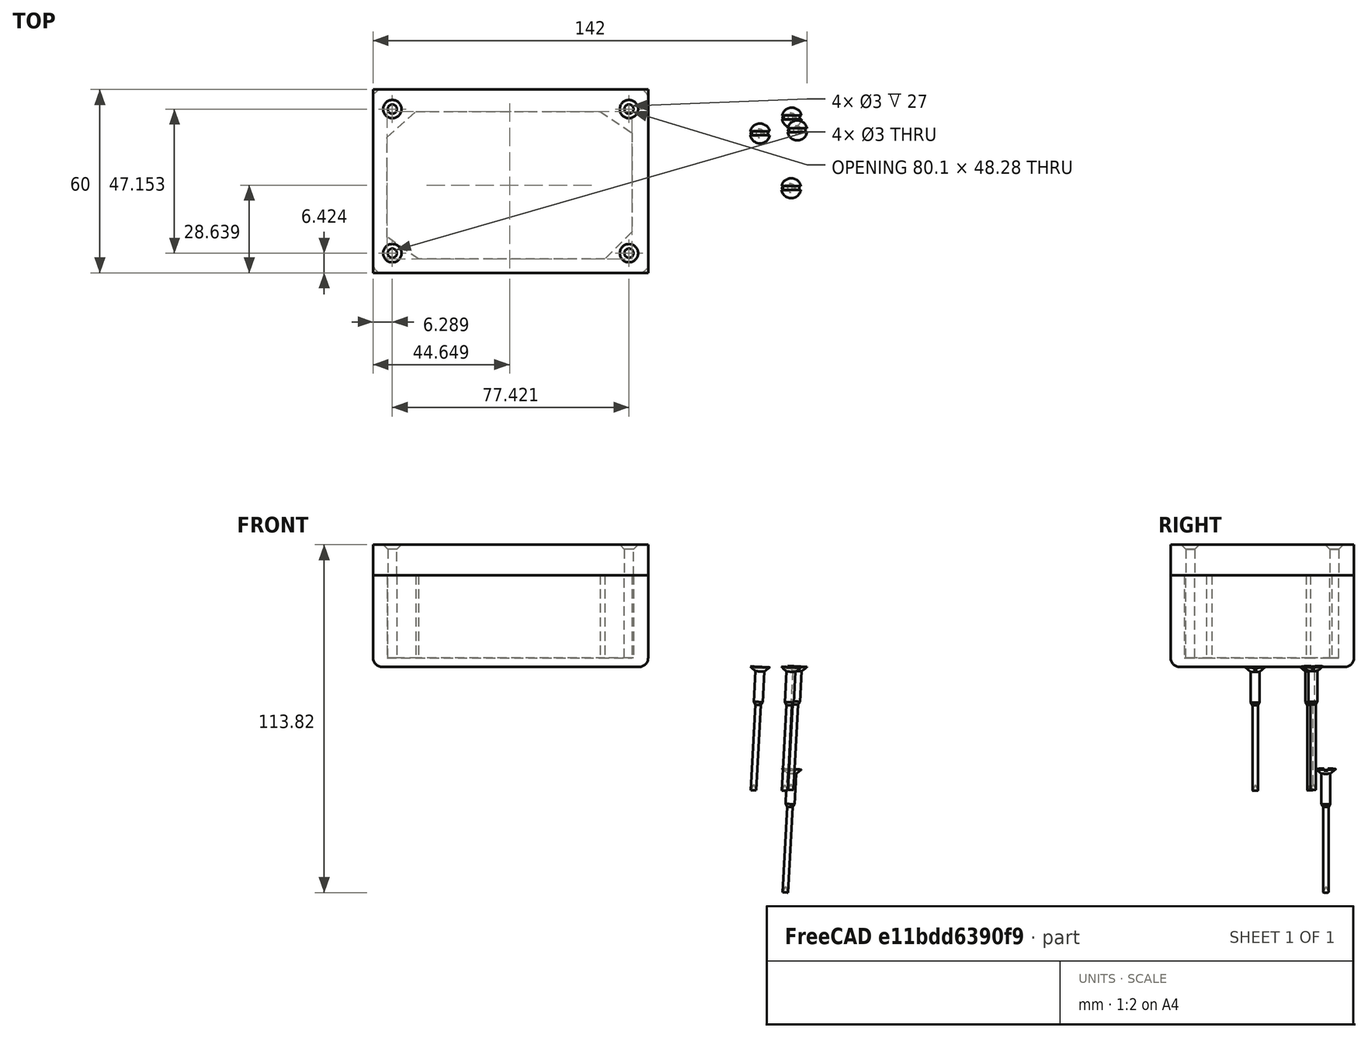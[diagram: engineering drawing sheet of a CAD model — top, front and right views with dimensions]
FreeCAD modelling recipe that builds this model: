
FCSTD DOCUMENT  (FreeCAD 0.18.4R)
Label: plastic_case3
License: All rights reserved
LicenseURL: http://en.wikipedia.org/wiki/All_rights_reserved
objects: Sketcher::SketchObject×16, TechDraw::DrawViewDimension×8, PartDesign::Body×7, PartDesign::Pocket×7, PartDesign::Revolution×4, TechDraw::DrawViewPart×3, PartDesign::Pad×2, PartDesign::Fillet×2, PartDesign::ShapeBinder×1, PartDesign::Chamfer×1, TechDraw::DrawSVGTemplate×1, TechDraw::DrawViewAnnotation×1, TechDraw::DrawPage×1
note: 53 computed .brp shape members not serialized (recipe doc carries the construction recipe); baked Part::Feature solids carry a one-line shape summary decoded from their .brp

FEATURE [Sketcher::SketchObject] Sketch
  MapMode = 5
  Support = -> [XY_Plane]
  sketch-geometry (4):
    g0: LineSegment StartX=-45 StartY=30 StartZ=0 EndX=45 EndY=30 EndZ=0
    g1: LineSegment StartX=45 StartY=30 StartZ=0 EndX=45 EndY=-30 EndZ=0
    g2: LineSegment StartX=45 StartY=-30 StartZ=0 EndX=-45 EndY=-30 EndZ=0
    g3: LineSegment StartX=-45 StartY=-30 StartZ=0 EndX=-45 EndY=30 EndZ=0
  constraints (12):
    c: Coincident(g0,g1)
    c: Coincident(g1,g2)
    c: Coincident(g2,g3)
    c: Coincident(g3,g0)
    c: Horizontal(g0)
    c: Horizontal(g2)
    c: Vertical(g1)
    c: Vertical(g3)
    c: DistanceX(g0) = 45
    c: DistanceY(g0) = 30
    c: DistanceX(g0,g0) = 90
    c: DistanceY(g1,g0) = 60
FEATURE [PartDesign::Pad] Pad
  Length = 30
  Length2 = 100
  Profile = -> Sketch
  Type = 0
FEATURE [PartDesign::ShapeBinder] CopyPad
  Placement = pos=(0,0,30) rot=(0,0,1;0rad)
  TraceSupport = false
FEATURE [Sketcher::SketchObject] Sketch001
  MapMode = 5
  Placement = pos=(0,0,30) rot=(0,0,1;0rad)
  Support = -> [CopyPad]
  sketch-geometry (12):
    g0: LineSegment StartX=-40.4009 StartY=14.4063 StartZ=0 EndX=-31.033 EndY=22.7794 EndZ=0
    g1: LineSegment StartX=-31.033 StartY=22.7794 StartZ=0 EndX=29.2768 EndY=22.7794 EndZ=0
    g2: LineSegment StartX=29.2768 StartY=22.7794 StartZ=0 EndX=39.6991 EndY=15.7622 EndZ=0
    g3: LineSegment StartX=39.6991 StartY=15.7622 StartZ=0 EndX=39.6991 EndY=-16.5719 EndZ=0
    g4: LineSegment StartX=39.6991 StartY=-16.5719 StartZ=0 EndX=30.8591 EndY=-25.5006 EndZ=0
    g5: LineSegment StartX=30.8591 StartY=-25.5006 StartZ=0 EndX=-30.0809 EndY=-25.5006 EndZ=0
    g6: LineSegment StartX=-30.0809 StartY=-25.5006 StartZ=0 EndX=-40.4009 EndY=-18.3337 EndZ=0
    g7: LineSegment StartX=-40.4009 StartY=-18.3337 StartZ=0 EndX=-40.4009 EndY=14.4063 EndZ=0
    g8: Circle CenterX=38.7106 CenterY=23.5763 CenterZ=0 NormalX=0 NormalY=0 NormalZ=1 AngleXU=0 Radius=1.5
    g9: Circle CenterX=-38.7106 CenterY=23.5763 CenterZ=0 NormalX=0 NormalY=0 NormalZ=1 AngleXU=0 Radius=1.5
    g10: Circle CenterX=-38.7106 CenterY=-23.5763 CenterZ=0 NormalX=0 NormalY=0 NormalZ=1 AngleXU=0 Radius=1.5
    g11: Circle CenterX=38.7106 CenterY=-23.5763 CenterZ=0 NormalX=0 NormalY=0 NormalZ=1 AngleXU=0 Radius=1.5
  constraints (33):
    c: Coincident(g0,g1)
    c: Coincident(g1,g2)
    c: Coincident(g2,g3)
    c: Coincident(g3,g4)
    c: Coincident(g4,g5)
    c: Coincident(g5,g6)
    c: Coincident(g6,g7)
    c: Coincident(g7,g0)
    c: Horizontal(g1)
    c: Vertical(g3)
    c: Horizontal(g5)
    c: Vertical(g7)
    c: DistanceX(g4,g4) = 8.84
    c: Equal(g4,g2)
    c: Equal(g0,g4)
    c: Equal(g6,g4)
    c: DistanceX(g1) = 29.2768
    c: DistanceY(g1) = 22.7794
    c: DistanceX(g2) = 39.6991
    c: DistanceY(g2) = 15.7622
    c: DistanceX(g5,g5) = 60.94
    c: DistanceY(g7,g7) = 32.74
    c: DistanceY(g5,g0) = 48.28
    c: DistanceX(g0,g2) = 80.1
    c: Radius(g8) = 1.5
    c: Equal(g8,g9)
    c: Equal(g8,g11)
    c: Equal(g8,g10)
    c: DistanceX(g8) = 38.7106
    c: DistanceY(g8) = 23.5763
    c: Symmetric(g8,g9,g-2)
    c: Symmetric(g8,g11,g-1)
    c: Symmetric(g9,g10,g-1)
FEATURE [PartDesign::Body] Body001
  Group = -> [CopyPad,Sketch001]
  Origin = -> Origin001
FEATURE [Sketcher::SketchObject] CopySketch001
  Placement = pos=(0,0,30) rot=(0,0,1;0rad)
  sketch-geometry (12):
    g0: LineSegment StartX=-40.4009 StartY=14.4063 StartZ=0 EndX=-31.033 EndY=22.7794 EndZ=0
    g1: LineSegment StartX=-31.033 StartY=22.7794 StartZ=0 EndX=29.2768 EndY=22.7794 EndZ=0
    g2: LineSegment StartX=29.2768 StartY=22.7794 StartZ=0 EndX=39.6991 EndY=15.7622 EndZ=0
    g3: LineSegment StartX=39.6991 StartY=15.7622 StartZ=0 EndX=39.6991 EndY=-16.5719 EndZ=0
    g4: LineSegment StartX=39.6991 StartY=-16.5719 StartZ=0 EndX=30.8591 EndY=-25.5006 EndZ=0
    g5: LineSegment StartX=30.8591 StartY=-25.5006 StartZ=0 EndX=-30.0809 EndY=-25.5006 EndZ=0
    g6: LineSegment StartX=-30.0809 StartY=-25.5006 StartZ=0 EndX=-40.4009 EndY=-18.3337 EndZ=0
    g7: LineSegment StartX=-40.4009 StartY=-18.3337 StartZ=0 EndX=-40.4009 EndY=14.4063 EndZ=0
    g8: Circle CenterX=38.7106 CenterY=23.5763 CenterZ=0 NormalX=0 NormalY=0 NormalZ=1 AngleXU=0 Radius=1.5
    g9: Circle CenterX=-38.7106 CenterY=23.5763 CenterZ=0 NormalX=0 NormalY=0 NormalZ=1 AngleXU=0 Radius=1.5
    g10: Circle CenterX=-38.7106 CenterY=-23.5763 CenterZ=0 NormalX=0 NormalY=0 NormalZ=1 AngleXU=0 Radius=1.5
    g11: Circle CenterX=38.7106 CenterY=-23.5763 CenterZ=0 NormalX=0 NormalY=0 NormalZ=1 AngleXU=0 Radius=1.5
  constraints (33):
    c: Coincident(g0,g1)
    c: Coincident(g1,g2)
    c: Coincident(g2,g3)
    c: Coincident(g3,g4)
    c: Coincident(g4,g5)
    c: Coincident(g5,g6)
    c: Coincident(g6,g7)
    c: Coincident(g7,g0)
    c: Horizontal(g1)
    c: Vertical(g3)
    c: Horizontal(g5)
    c: Vertical(g7)
    c: DistanceX(g4,g4) = 8.84
    c: Equal(g4,g2)
    c: Equal(g0,g4)
    c: Equal(g6,g4)
    c: DistanceX(g1) = 29.2768
    c: DistanceY(g1) = 22.7794
    c: DistanceX(g2) = 39.6991
    c: DistanceY(g2) = 15.7622
    c: DistanceX(g5,g5) = 60.94
    c: DistanceY(g7,g7) = 32.74
    c: DistanceY(g5,g0) = 48.28
    c: DistanceX(g0,g2) = 80.1
    c: Radius(g8) = 1.5
    c: Equal(g8,g9)
    c: Equal(g8,g11)
    c: Equal(g8,g10)
    c: DistanceX(g8) = 38.7106
    c: DistanceY(g8) = 23.5763
    c: Symmetric(g8,g9,g-2)
    c: Symmetric(g8,g11,g-1)
    c: Symmetric(g9,g10,g-1)
FEATURE [PartDesign::Pocket] Pocket
  BaseFeature = -> Pad
  Length = 27
  Length2 = 100
  Profile = -> CopySketch001
  Type = 0
FEATURE [PartDesign::Fillet] Fillet
  Base = -> Pocket [Edge5,Edge1,Edge8,Edge2]
  BaseFeature = -> Pocket
  Radius = 3
FEATURE [PartDesign::Fillet] Fillet001
  Base = -> Fillet [Edge8,Edge1,Edge7,Edge11,Edge10,Edge6,Edge5,Edge9]
  BaseFeature = -> Fillet
  Radius = 3
FEATURE [PartDesign::Body] Body
  Group = -> [Sketch,Pad,CopySketch001,Pocket,Fillet,Fillet001]
  Origin = -> Origin
  Tip = -> Fillet001
FEATURE [Sketcher::SketchObject] Sketch002
  MapMode = 5
  Placement = pos=(0,0,30) rot=(0,0,1;0rad)
  sketch-geometry (4):
    g0: LineSegment StartX=-45 StartY=30 StartZ=0 EndX=45 EndY=30 EndZ=0
    g1: LineSegment StartX=45 StartY=30 StartZ=0 EndX=45 EndY=-30 EndZ=0
    g2: LineSegment StartX=45 StartY=-30 StartZ=0 EndX=-45 EndY=-30 EndZ=0
    g3: LineSegment StartX=-45 StartY=-30 StartZ=0 EndX=-45 EndY=30 EndZ=0
  constraints (12):
    c: Coincident(g0,g1)
    c: Coincident(g1,g2)
    c: Coincident(g2,g3)
    c: Coincident(g3,g0)
    c: Horizontal(g0)
    c: Horizontal(g2)
    c: Vertical(g1)
    c: Vertical(g3)
    c: DistanceX(g0) = 45
    c: DistanceY(g0) = 30
    c: DistanceX(g0,g0) = 90
    c: DistanceY(g1,g0) = 60
FEATURE [PartDesign::Pad] Pad001
  Length = 10
  Length2 = 100
  Placement = pos=(0,0,30) rot=(0,0,1;0rad)
  Profile = -> Sketch002
  Type = 0
FEATURE [Sketcher::SketchObject] CopySketch002
  Placement = pos=(0,0,30) rot=(0,0,1;0rad)
  sketch-geometry (8):
    g0: LineSegment StartX=-40.4009 StartY=14.4063 StartZ=0 EndX=-30.0832 EndY=22.7794 EndZ=0
    g1: LineSegment StartX=-30.0832 StartY=22.7794 StartZ=0 EndX=29.2768 EndY=22.7794 EndZ=0
    g2: LineSegment StartX=29.2768 StartY=22.7794 StartZ=0 EndX=39.6991 EndY=15.7622 EndZ=0
    g3: LineSegment StartX=39.6991 StartY=15.7622 StartZ=0 EndX=39.6991 EndY=-16.5719 EndZ=0
    g4: LineSegment StartX=39.6991 StartY=-16.5719 StartZ=0 EndX=30.8591 EndY=-25.5006 EndZ=0
    g5: LineSegment StartX=30.8591 StartY=-25.5006 StartZ=0 EndX=-30.0809 EndY=-25.5006 EndZ=0
    g6: LineSegment StartX=-30.0809 StartY=-25.5006 StartZ=0 EndX=-40.4009 EndY=-18.3337 EndZ=0
    g7: LineSegment StartX=-40.4009 StartY=-18.3337 StartZ=0 EndX=-40.4009 EndY=14.4063 EndZ=0
  constraints (24):
    c: Coincident(g0,g1)
    c: Coincident(g1,g2)
    c: Coincident(g2,g3)
    c: Coincident(g3,g4)
    c: Coincident(g4,g5)
    c: Coincident(g5,g6)
    c: Coincident(g6,g7)
    c: Coincident(g7,g0)
    c: Horizontal(g1)
    c: Vertical(g3)
    c: Horizontal(g5)
    c: Vertical(g7)
    c: DistanceX(g4,g4) = 8.84
    c: Equal(g4,g2)
    c: Equal(g6,g4)
    c: DistanceX(g1) = 29.2768
    c: DistanceY(g1) = 22.7794
    c: DistanceX(g2) = 39.6991
    c: DistanceY(g2) = 15.7622
    c: DistanceX(g5,g5) = 60.94
    c: DistanceY(g7,g7) = 32.74
    c: DistanceY(g5,g0) = 48.28
    c: DistanceX(g0,g2) = 80.1
    c: DistanceX(g0,g1) = 59.36
FEATURE [Sketcher::SketchObject] CopyCopySketch002
  Placement = pos=(0,0,30) rot=(0,0,1;0rad)
  sketch-geometry (8):
    g0: LineSegment StartX=-40.4009 StartY=14.4063 StartZ=0 EndX=-30.0832 EndY=22.7794 EndZ=0
    g1: LineSegment StartX=-30.0832 StartY=22.7794 StartZ=0 EndX=29.2768 EndY=22.7794 EndZ=0
    g2: LineSegment StartX=29.2768 StartY=22.7794 StartZ=0 EndX=39.6991 EndY=15.7622 EndZ=0
    g3: LineSegment StartX=39.6991 StartY=15.7622 StartZ=0 EndX=39.6991 EndY=-16.5719 EndZ=0
    g4: LineSegment StartX=39.6991 StartY=-16.5719 StartZ=0 EndX=30.8591 EndY=-25.5006 EndZ=0
    g5: LineSegment StartX=30.8591 StartY=-25.5006 StartZ=0 EndX=-30.0809 EndY=-25.5006 EndZ=0
    g6: LineSegment StartX=-30.0809 StartY=-25.5006 StartZ=0 EndX=-40.4009 EndY=-18.3337 EndZ=0
    g7: LineSegment StartX=-40.4009 StartY=-18.3337 StartZ=0 EndX=-40.4009 EndY=14.4063 EndZ=0
  constraints (24):
    c: Coincident(g0,g1)
    c: Coincident(g1,g2)
    c: Coincident(g2,g3)
    c: Coincident(g3,g4)
    c: Coincident(g4,g5)
    c: Coincident(g5,g6)
    c: Coincident(g6,g7)
    c: Coincident(g7,g0)
    c: Horizontal(g1)
    c: Vertical(g3)
    c: Horizontal(g5)
    c: Vertical(g7)
    c: DistanceX(g4,g4) = 8.84
    c: Equal(g4,g2)
    c: Equal(g6,g4)
    c: DistanceX(g1) = 29.2768
    c: DistanceY(g1) = 22.7794
    c: DistanceX(g2) = 39.6991
    c: DistanceY(g2) = 15.7622
    c: DistanceX(g5,g5) = 60.94
    c: DistanceY(g7,g7) = 32.74
    c: DistanceY(g5,g0) = 48.28
    c: DistanceX(g0,g2) = 80.1
    c: DistanceX(g0,g1) = 59.36
FEATURE [PartDesign::Pocket] Pocket001
  BaseFeature = -> Pad001
  Length = 7
  Length2 = 100
  Placement = pos=(0,0,30) rot=(0,0,1;0rad)
  Profile = -> CopyCopySketch002
  Type = 0
FEATURE [Sketcher::SketchObject] CopySketch003
  Placement = pos=(0,0,30) rot=(0,0,1;0rad)
  sketch-geometry (4):
    g0: Circle CenterX=38.7106 CenterY=23.5763 CenterZ=0 NormalX=0 NormalY=0 NormalZ=1 AngleXU=0 Radius=1.5
    g1: Circle CenterX=-38.7106 CenterY=23.5763 CenterZ=0 NormalX=0 NormalY=0 NormalZ=1 AngleXU=0 Radius=1.5
    g2: Circle CenterX=-38.7106 CenterY=-23.5763 CenterZ=0 NormalX=0 NormalY=0 NormalZ=1 AngleXU=0 Radius=1.5
    g3: Circle CenterX=38.7106 CenterY=-23.5763 CenterZ=0 NormalX=0 NormalY=0 NormalZ=1 AngleXU=0 Radius=1.5
  constraints (9):
    c: Radius(g0) = 1.5
    c: Equal(g0,g1)
    c: Equal(g0,g3)
    c: Equal(g0,g2)
    c: DistanceX(g0) = 38.7106
    c: DistanceY(g0) = 23.5763
    c: Symmetric(g0,g1,g-2)
    c: Symmetric(g0,g3,g-1)
    c: Symmetric(g1,g2,g-1)
FEATURE [Sketcher::SketchObject] CopyCopySketch003
  Placement = pos=(0,0,30) rot=(0,0,1;0rad)
  sketch-geometry (4):
    g0: Circle CenterX=38.7106 CenterY=23.5763 CenterZ=0 NormalX=0 NormalY=0 NormalZ=1 AngleXU=0 Radius=1.5
    g1: Circle CenterX=-38.7106 CenterY=23.5763 CenterZ=0 NormalX=0 NormalY=0 NormalZ=1 AngleXU=0 Radius=1.5
    g2: Circle CenterX=-38.7106 CenterY=-23.5763 CenterZ=0 NormalX=0 NormalY=0 NormalZ=1 AngleXU=0 Radius=1.5
    g3: Circle CenterX=38.7106 CenterY=-23.5763 CenterZ=0 NormalX=0 NormalY=0 NormalZ=1 AngleXU=0 Radius=1.5
  constraints (9):
    c: Radius(g0) = 1.5
    c: Equal(g0,g1)
    c: Equal(g0,g3)
    c: Equal(g0,g2)
    c: DistanceX(g0) = 38.7106
    c: DistanceY(g0) = 23.5763
    c: Symmetric(g0,g1,g-2)
    c: Symmetric(g0,g3,g-1)
    c: Symmetric(g1,g2,g-1)
FEATURE [PartDesign::Pocket] Pocket002
  BaseFeature = -> Pocket001
  Length = 50
  Length2 = 100
  Placement = pos=(0,0,30) rot=(0,0,1;0rad)
  Profile = -> CopyCopySketch003
  Reversed = true
  Type = 0
FEATURE [PartDesign::Chamfer] Chamfer
  Base = -> Pocket002 [Edge26,Edge25,Edge28,Edge27]
  BaseFeature = -> Pocket002
  Placement = pos=(0,0,30) rot=(0,0,1;0rad)
  Size = 1.5
FEATURE [PartDesign::Body] Body002
  Group = -> [Sketch002,Pad001,Pocket001,Pocket002,Chamfer]
  Origin = -> Origin002
  Tip = -> Chamfer
FEATURE [Sketcher::SketchObject] Sketch003
  MapMode = 5
  Support = -> [XY_Plane003]
  sketch-geometry (7):
    g0: LineSegment StartX=0 StartY=0 StartZ=0 EndX=0 EndY=3.25 EndZ=0
    g1: LineSegment StartX=0 StartY=3.25 StartZ=0 EndX=1.47 EndY=1.46 EndZ=0
    g2: LineSegment StartX=40.42 StartY=0.91 StartZ=0 EndX=38.54 EndY=0 EndZ=0
    g3: LineSegment StartX=38.54 StartY=0 StartZ=0 EndX=0 EndY=0 EndZ=0
    g4: LineSegment StartX=1.47 StartY=1.46 StartZ=0 EndX=11.47 EndY=1.46 EndZ=0
    g5: LineSegment StartX=11.47 StartY=1.46 StartZ=0 EndX=12.42 EndY=0.91 EndZ=0
    g6: LineSegment StartX=12.42 StartY=0.91 StartZ=0 EndX=40.42 EndY=0.91 EndZ=0
  constraints (20):
    c: Coincident(g0,g1)
    c: Coincident(g2,g3)
    c: Coincident(g3,g0)
    c: Coincident(g0,g-1)
    c: Coincident(g4,g5)
    c: Coincident(g5,g6)
    c: Coincident(g2,g6)
    c: DistanceY(g0,g0) = 3.25
    c: DistanceX(g1,g4) = 10
    c: Coincident(g4,g1)
    c: DistanceX(g5,g2) = 28
    c: DistanceX(g0,g2) = 38.54
    c: DistanceY(g2,g2) = 0.91
    c: DistanceY(g1,g0) = 1.79
    c: DistanceX(g4,g5) = 0.95
    c: Horizontal(g3)
    c: Horizontal(g6)
    c: Horizontal(g4)
    c: Vertical(g0)
    c: DistanceX(g0,g1) = 1.47
FEATURE [PartDesign::Revolution] Revolution
  Angle = 360
  Axis = (1,0,0)
  Base = (0,0,0)
  Profile = -> Sketch003
  ReferenceAxis = -> X_Axis003
FEATURE [Sketcher::SketchObject] Sketch004
  MapMode = 5
  Placement = pos=(0,0,0) rot=(0.57735,-0.57735,-0.57735;2.0944rad)
  Support = -> [Revolution]
  sketch-geometry (4):
    g0: LineSegment StartX=-0.677328 StartY=3.3113 StartZ=0 EndX=0.602672 EndY=3.3113 EndZ=0
    g1: LineSegment StartX=0.602672 StartY=3.3113 StartZ=0 EndX=0.602672 EndY=-3.2887 EndZ=0
    g2: LineSegment StartX=0.602672 StartY=-3.2887 StartZ=0 EndX=-0.677328 EndY=-3.2887 EndZ=0
    g3: LineSegment StartX=-0.677328 StartY=-3.2887 StartZ=0 EndX=-0.677328 EndY=3.3113 EndZ=0
  constraints (12):
    c: Coincident(g0,g1)
    c: Coincident(g1,g2)
    c: Coincident(g2,g3)
    c: Coincident(g3,g0)
    c: Horizontal(g0)
    c: Horizontal(g2)
    c: Vertical(g1)
    c: Vertical(g3)
    c: DistanceX(g0) = 0.602672
    c: DistanceY(g0) = 3.3113
    c: DistanceY(g1,g1) = 6.6
    c: DistanceX(g2,g2) = 1.28
FEATURE [PartDesign::Pocket] Pocket003
  BaseFeature = -> Revolution
  Length = 0.5
  Length2 = 100
  Profile = -> Sketch004
  Type = 0
FEATURE [PartDesign::Body] Body003
  Group = -> [Sketch003,Revolution,Sketch004,Pocket003]
  Origin = -> Origin003
  Placement = pos=(92.01,20.8058,-33.41) rot=(0,1,0;1.62316rad)
  Tip = -> Pocket003
FEATURE [Sketcher::SketchObject] Sketch005
  MapMode = 5
  Support = -> [XY_Plane004]
  sketch-geometry (7):
    g0: LineSegment StartX=0 StartY=0 StartZ=0 EndX=0 EndY=3.25 EndZ=0
    g1: LineSegment StartX=0 StartY=3.25 StartZ=0 EndX=1.47 EndY=1.46 EndZ=0
    g2: LineSegment StartX=40.42 StartY=0.91 StartZ=0 EndX=38.54 EndY=0 EndZ=0
    g3: LineSegment StartX=38.54 StartY=0 StartZ=0 EndX=0 EndY=0 EndZ=0
    g4: LineSegment StartX=1.47 StartY=1.46 StartZ=0 EndX=11.47 EndY=1.46 EndZ=0
    g5: LineSegment StartX=11.47 StartY=1.46 StartZ=0 EndX=12.42 EndY=0.91 EndZ=0
    g6: LineSegment StartX=12.42 StartY=0.91 StartZ=0 EndX=40.42 EndY=0.91 EndZ=0
  constraints (20):
    c: Coincident(g0,g1)
    c: Coincident(g2,g3)
    c: Coincident(g3,g0)
    c: Coincident(g0,g-1)
    c: Coincident(g4,g5)
    c: Coincident(g5,g6)
    c: Coincident(g2,g6)
    c: DistanceY(g0,g0) = 3.25
    c: DistanceX(g1,g4) = 10
    c: Coincident(g4,g1)
    c: DistanceX(g5,g2) = 28
    c: DistanceX(g0,g2) = 38.54
    c: DistanceY(g2,g2) = 0.91
    c: DistanceY(g1,g0) = 1.79
    c: DistanceX(g4,g5) = 0.95
    c: Horizontal(g3)
    c: Horizontal(g6)
    c: Horizontal(g4)
    c: Vertical(g0)
    c: DistanceX(g0,g1) = 1.47
FEATURE [PartDesign::Revolution] Revolution001
  Angle = 360
  Axis = (1,0,0)
  Base = (0,0,0)
  Profile = -> Sketch005
  ReferenceAxis = -> X_Axis004
FEATURE [Sketcher::SketchObject] Sketch006
  MapMode = 5
  Placement = pos=(0,0,0) rot=(0.57735,-0.57735,-0.57735;2.0944rad)
  Support = -> [Revolution001]
  sketch-geometry (4):
    g0: LineSegment StartX=-0.677328 StartY=3.3113 StartZ=0 EndX=0.602672 EndY=3.3113 EndZ=0
    g1: LineSegment StartX=0.602672 StartY=3.3113 StartZ=0 EndX=0.602672 EndY=-3.2887 EndZ=0
    g2: LineSegment StartX=0.602672 StartY=-3.2887 StartZ=0 EndX=-0.677328 EndY=-3.2887 EndZ=0
    g3: LineSegment StartX=-0.677328 StartY=-3.2887 StartZ=0 EndX=-0.677328 EndY=3.3113 EndZ=0
  constraints (12):
    c: Coincident(g0,g1)
    c: Coincident(g1,g2)
    c: Coincident(g2,g3)
    c: Coincident(g3,g0)
    c: Horizontal(g0)
    c: Horizontal(g2)
    c: Vertical(g1)
    c: Vertical(g3)
    c: DistanceX(g0) = 0.602672
    c: DistanceY(g0) = 3.3113
    c: DistanceY(g1,g1) = 6.6
    c: DistanceX(g2,g2) = 1.28
FEATURE [PartDesign::Pocket] Pocket004
  BaseFeature = -> Revolution001
  Length = 0.5
  Length2 = 100
  Profile = -> Sketch006
  Type = 0
FEATURE [PartDesign::Body] Body004
  Group = -> [Sketch005,Revolution001,Sketch006,Pocket004]
  Origin = -> Origin004
  Placement = pos=(91.81,-2.31,-0.09509) rot=(0,1,0;1.62316rad)
  Tip = -> Pocket004
FEATURE [Sketcher::SketchObject] Sketch007
  MapMode = 5
  Support = -> [XY_Plane005]
  sketch-geometry (7):
    g0: LineSegment StartX=0 StartY=0 StartZ=0 EndX=0 EndY=3.25 EndZ=0
    g1: LineSegment StartX=0 StartY=3.25 StartZ=0 EndX=1.47 EndY=1.46 EndZ=0
    g2: LineSegment StartX=40.42 StartY=0.91 StartZ=0 EndX=38.54 EndY=0 EndZ=0
    g3: LineSegment StartX=38.54 StartY=0 StartZ=0 EndX=0 EndY=0 EndZ=0
    g4: LineSegment StartX=1.47 StartY=1.46 StartZ=0 EndX=11.47 EndY=1.46 EndZ=0
    g5: LineSegment StartX=11.47 StartY=1.46 StartZ=0 EndX=12.42 EndY=0.91 EndZ=0
    g6: LineSegment StartX=12.42 StartY=0.91 StartZ=0 EndX=40.42 EndY=0.91 EndZ=0
  constraints (20):
    c: Coincident(g0,g1)
    c: Coincident(g2,g3)
    c: Coincident(g3,g0)
    c: Coincident(g0,g-1)
    c: Coincident(g4,g5)
    c: Coincident(g5,g6)
    c: Coincident(g2,g6)
    c: DistanceY(g0,g0) = 3.25
    c: DistanceX(g1,g4) = 10
    c: Coincident(g4,g1)
    c: DistanceX(g5,g2) = 28
    c: DistanceX(g0,g2) = 38.54
    c: DistanceY(g2,g2) = 0.91
    c: DistanceY(g1,g0) = 1.79
    c: DistanceX(g4,g5) = 0.95
    c: Horizontal(g3)
    c: Horizontal(g6)
    c: Horizontal(g4)
    c: Vertical(g0)
    c: DistanceX(g0,g1) = 1.47
FEATURE [PartDesign::Revolution] Revolution002
  Angle = 360
  Axis = (1,0,0)
  Base = (0,0,0)
  Profile = -> Sketch007
  ReferenceAxis = -> X_Axis005
FEATURE [Sketcher::SketchObject] Sketch008
  MapMode = 5
  Placement = pos=(0,0,0) rot=(0.57735,-0.57735,-0.57735;2.0944rad)
  Support = -> [Revolution002]
  sketch-geometry (4):
    g0: LineSegment StartX=-0.677328 StartY=3.3113 StartZ=0 EndX=0.602672 EndY=3.3113 EndZ=0
    g1: LineSegment StartX=0.602672 StartY=3.3113 StartZ=0 EndX=0.602672 EndY=-3.2887 EndZ=0
    g2: LineSegment StartX=0.602672 StartY=-3.2887 StartZ=0 EndX=-0.677328 EndY=-3.2887 EndZ=0
    g3: LineSegment StartX=-0.677328 StartY=-3.2887 StartZ=0 EndX=-0.677328 EndY=3.3113 EndZ=0
  constraints (12):
    c: Coincident(g0,g1)
    c: Coincident(g1,g2)
    c: Coincident(g2,g3)
    c: Coincident(g3,g0)
    c: Horizontal(g0)
    c: Horizontal(g2)
    c: Vertical(g1)
    c: Vertical(g3)
    c: DistanceX(g0) = 0.602672
    c: DistanceY(g0) = 3.3113
    c: DistanceY(g1,g1) = 6.6
    c: DistanceX(g2,g2) = 1.28
FEATURE [PartDesign::Pocket] Pocket005
  BaseFeature = -> Revolution002
  Length = 0.5
  Length2 = 100
  Profile = -> Sketch008
  Type = 0
FEATURE [PartDesign::Body] Body005
  Group = -> [Sketch007,Revolution002,Sketch008,Pocket005]
  Origin = -> Origin005
  Placement = pos=(93.81,16.6,0.17) rot=(0,1,0;1.62316rad)
  Tip = -> Pocket005
FEATURE [Sketcher::SketchObject] Sketch010
  MapMode = 5
  Support = -> [XY_Plane006]
  sketch-geometry (7):
    g0: LineSegment StartX=0 StartY=0 StartZ=0 EndX=0 EndY=3.25 EndZ=0
    g1: LineSegment StartX=0 StartY=3.25 StartZ=0 EndX=1.47 EndY=1.46 EndZ=0
    g2: LineSegment StartX=40.42 StartY=0.91 StartZ=0 EndX=38.54 EndY=0 EndZ=0
    g3: LineSegment StartX=38.54 StartY=0 StartZ=0 EndX=0 EndY=0 EndZ=0
    g4: LineSegment StartX=1.47 StartY=1.46 StartZ=0 EndX=11.47 EndY=1.46 EndZ=0
    g5: LineSegment StartX=11.47 StartY=1.46 StartZ=0 EndX=12.42 EndY=0.91 EndZ=0
    g6: LineSegment StartX=12.42 StartY=0.91 StartZ=0 EndX=40.42 EndY=0.91 EndZ=0
  constraints (20):
    c: Coincident(g0,g1)
    c: Coincident(g2,g3)
    c: Coincident(g3,g0)
    c: Coincident(g0,g-1)
    c: Coincident(g4,g5)
    c: Coincident(g5,g6)
    c: Coincident(g2,g6)
    c: DistanceY(g0,g0) = 3.25
    c: DistanceX(g1,g4) = 10
    c: Coincident(g4,g1)
    c: DistanceX(g5,g2) = 28
    c: DistanceX(g0,g2) = 38.54
    c: DistanceY(g2,g2) = 0.91
    c: DistanceY(g1,g0) = 1.79
    c: DistanceX(g4,g5) = 0.95
    c: Horizontal(g3)
    c: Horizontal(g6)
    c: Horizontal(g4)
    c: Vertical(g0)
    c: DistanceX(g0,g1) = 1.47
FEATURE [PartDesign::Revolution] Revolution003
  Angle = 360
  Axis = (1,0,0)
  Base = (0,0,0)
  Profile = -> Sketch010
  ReferenceAxis = -> X_Axis006
FEATURE [Sketcher::SketchObject] Sketch009
  MapMode = 5
  Placement = pos=(0,0,0) rot=(0.57735,-0.57735,-0.57735;2.0944rad)
  Support = -> [Revolution003]
  sketch-geometry (4):
    g0: LineSegment StartX=-0.677328 StartY=3.3113 StartZ=0 EndX=0.602672 EndY=3.3113 EndZ=0
    g1: LineSegment StartX=0.602672 StartY=3.3113 StartZ=0 EndX=0.602672 EndY=-3.2887 EndZ=0
    g2: LineSegment StartX=0.602672 StartY=-3.2887 StartZ=0 EndX=-0.677328 EndY=-3.2887 EndZ=0
    g3: LineSegment StartX=-0.677328 StartY=-3.2887 StartZ=0 EndX=-0.677328 EndY=3.3113 EndZ=0
  constraints (12):
    c: Coincident(g0,g1)
    c: Coincident(g1,g2)
    c: Coincident(g2,g3)
    c: Coincident(g3,g0)
    c: Horizontal(g0)
    c: Horizontal(g2)
    c: Vertical(g1)
    c: Vertical(g3)
    c: DistanceX(g0) = 0.602672
    c: DistanceY(g0) = 3.3113
    c: DistanceY(g1,g1) = 6.6
    c: DistanceX(g2,g2) = 1.28
FEATURE [PartDesign::Pocket] Pocket006
  BaseFeature = -> Revolution003
  Length = 0.5
  Length2 = 100
  Profile = -> Sketch009
  Type = 0
FEATURE [PartDesign::Body] Body006
  Group = -> [Sketch010,Revolution003,Sketch009,Pocket006]
  Origin = -> Origin006
  Placement = pos=(81.6,15.6,0.02081) rot=(0,1,0;1.62316rad)
  Tip = -> Pocket006
FEATURE [TechDraw::DrawSVGTemplate] Template
  EditableTexts = Designed_by_Name=Tsn; Drawing_number=Drawing number; FC-Date=04/22/2021; FC-SC=Scale; FC-SH=Sheet; FC-Title=Flex Robotics; Subtitle=Subtitle; Weight=Weight
  Height = 210
  Orientation = 1
  Width = 297
FEATURE [TechDraw::DrawViewPart] View
  CoarseView = false
  Direction = (-0.274,-0.494,0.825)
  Focus = 100
  HardHidden = false
  IsoCount = 0
  IsoHidden = false
  IsoVisible = false
  LockPosition = false
  Perspective = false
  Rotation = 0
  ScaleType = 0
  SeamHidden = false
  SeamVisible = false
  SmoothHidden = false
  SmoothVisible = false
  Source = -> [Body]
  X = 229.107
  Y = 147.737
FEATURE [TechDraw::DrawViewPart] View001
  CoarseView = false
  Direction = (-0.274,-0.494,0.825)
  Focus = 100
  HardHidden = false
  IsoCount = 0
  IsoHidden = false
  IsoVisible = false
  LockPosition = false
  Perspective = false
  Rotation = 0
  ScaleType = 0
  SeamHidden = false
  SeamVisible = false
  SmoothHidden = false
  SmoothVisible = false
  Source = -> [Body003]
  X = 24.1115
  Y = 42.8058
FEATURE [TechDraw::DrawViewPart] View002
  CoarseView = false
  Direction = (-0.274,-0.494,0.825)
  Focus = 100
  HardHidden = false
  IsoCount = 0
  IsoHidden = false
  IsoVisible = false
  LockPosition = false
  Perspective = false
  Rotation = 0
  ScaleType = 0
  SeamHidden = false
  SeamVisible = false
  SmoothHidden = false
  SmoothVisible = false
  Source = -> [Body002]
  X = 80.7662
  Y = 154.604
FEATURE [TechDraw::DrawViewDimension] Dimension
  Arbitrary = false
  FormatSpec = %.2f
  LockPosition = false
  MeasureType = 1
  OverTolerance = 0
  References2D = -> [View002]
  Rotation = 0
  ScaleType = 0
  Type = 1
  UnderTolerance = 0
  X = 22.357
  Y = -58.8576
FEATURE [TechDraw::DrawViewDimension] Dimension001
  Arbitrary = false
  FormatSpec = %.2f
  LockPosition = false
  MeasureType = 1
  OverTolerance = 0
  References2D = -> [View]
  Rotation = 0
  ScaleType = 0
  Type = 1
  UnderTolerance = 0
  X = 22.3445
  Y = -44.4327
FEATURE [TechDraw::DrawViewDimension] Dimension002
  Arbitrary = false
  FormatSpec = %.2f
  LockPosition = false
  MeasureType = 1
  OverTolerance = 0
  References2D = -> [View]
  Rotation = 0
  ScaleType = 0
  Type = 2
  UnderTolerance = 0
  X = -24.9386
  Y = -7.74164
FEATURE [TechDraw::DrawViewDimension] Dimension003
  Arbitrary = false
  FormatSpec = %.2f
  LockPosition = false
  MeasureType = 1
  OverTolerance = 0
  References2D = -> [View002]
  Rotation = 0
  ScaleType = 0
  Type = 2
  UnderTolerance = 0
  X = 63.7766
  Y = 20.3308
FEATURE [TechDraw::DrawViewDimension] Dimension004
  Arbitrary = false
  FormatSpec = %.2f
  LockPosition = false
  MeasureType = 1
  OverTolerance = 0
  References2D = -> [View001]
  Rotation = 0
  ScaleType = 0
  Type = 2
  UnderTolerance = 0
  X = 22.4233
  Y = -0.347762
FEATURE [TechDraw::DrawViewDimension] Dimension005
  Arbitrary = false
  FormatSpec = %.2f
  LockPosition = false
  MeasureType = 1
  OverTolerance = 0
  References2D = -> [View]
  Rotation = 0
  ScaleType = 0
  Type = 2
  UnderTolerance = 0
  X = -48.9801
  Y = -35.7627
FEATURE [TechDraw::DrawViewDimension] Dimension006
  Arbitrary = false
  FormatSpec = %.2f
  LockPosition = false
  MeasureType = 1
  OverTolerance = 0
  References2D = -> [View002]
  Rotation = 0
  ScaleType = 0
  Type = 2
  UnderTolerance = 0
  X = 63.4717
  Y = -26.047
FEATURE [TechDraw::DrawViewAnnotation] Annotation
  Font = osifont
  LineSpace = 80
  LockPosition = false
  MaxWidth = -1
  Rotation = 0
  ScaleType = 0
  Text = Top
  TextSize = 8
  TextStyle = 0
  X = 79.759
  Y = 163.165
FEATURE [TechDraw::DrawViewDimension] Dimension007
  Arbitrary = false
  FormatSpec = %.2f
  LockPosition = false
  MeasureType = 1
  OverTolerance = 0
  References2D = -> [View001]
  Rotation = 0
  ScaleType = 0
  Type = 1
  UnderTolerance = 0
  X = 25.6964
  Y = -18.4633
FEATURE [TechDraw::DrawPage] Page001
  KeepUpdated = true
  ProjectionType = 0
  Template = -> Template
  Views = -> [View,View001,View002,Dimension,Dimension001,Dimension002,Dimension003,Dimension004,Dimension005,Dimension006,Annotation,Dimension007]
